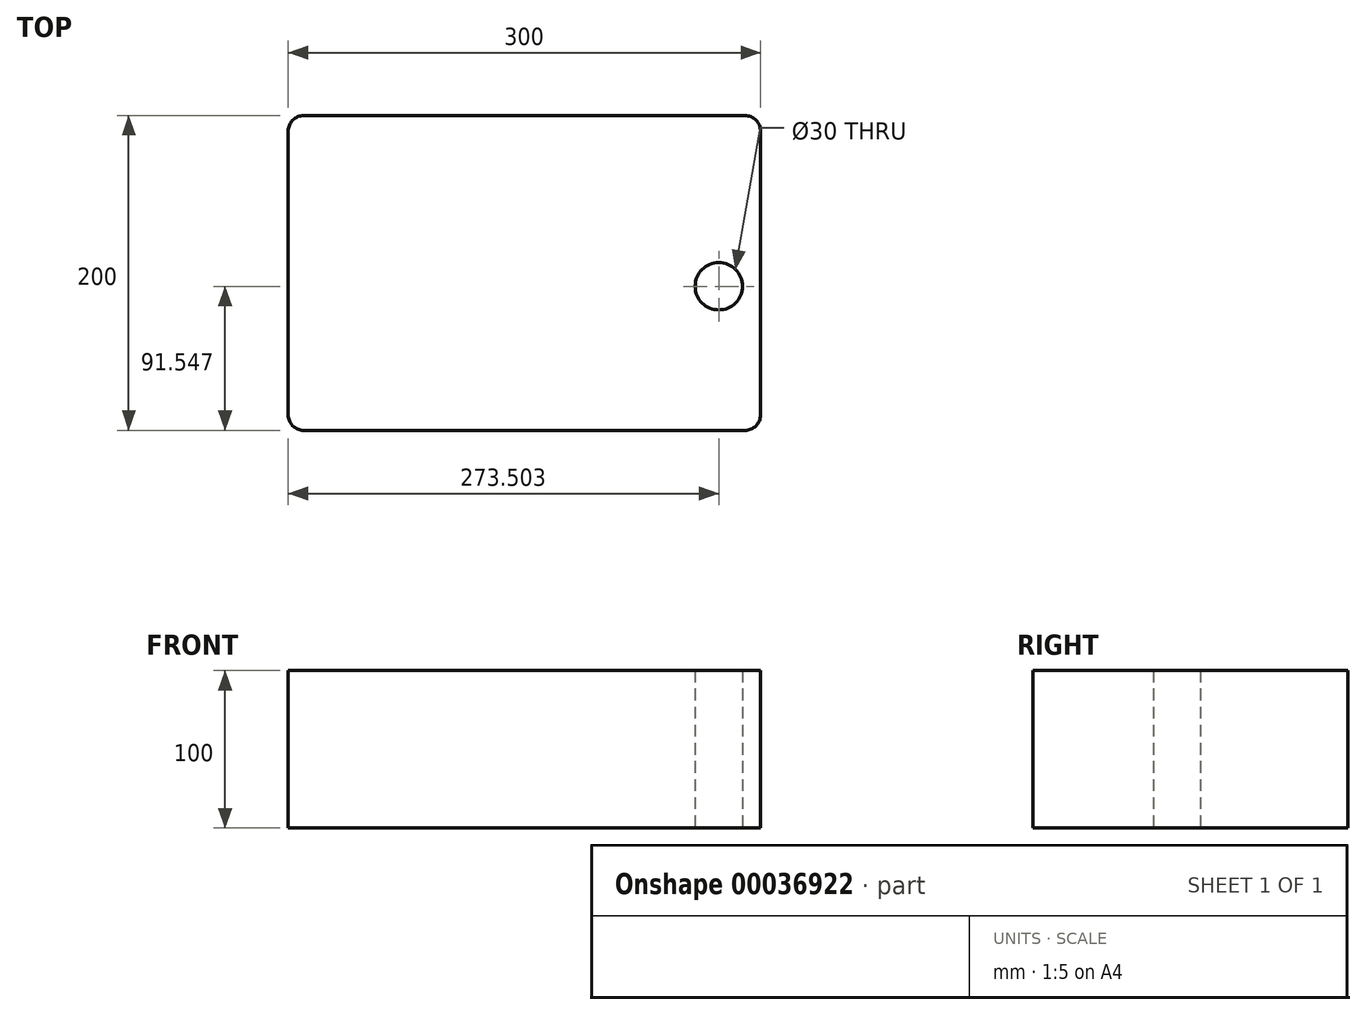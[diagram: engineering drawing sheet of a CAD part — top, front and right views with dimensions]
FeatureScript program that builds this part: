
annotation { "Feature Type Name" : "Feature", "Feature Type Description" : "" }
export const myFeature = defineFeature(function(context is Context, id is Id, definition is map)
    precondition{}
    {
        {
            var Q0;
            Q0=qCreatedBy(makeId("Top.planeOp"),FACE);
            var sketch = newSketch(context, id + "F0", { "sketchPlane" : qUnion([Q0])});
            skLineSegment(sketch, "E0.bottom", {"start": v(-149.02, 128.34) * mm, "end": v(150.98, 128.34) * mm});
            skLineSegment(sketch, "E0.top", {"start": v(-149.02, -71.66) * mm, "end": v(150.98, -71.66) * mm});
            skLineSegment(sketch, "E0.left", {"start": v(-149.02, 128.34) * mm, "end": v(-149.02, -71.66) * mm});
            skLineSegment(sketch, "E0.right", {"start": v(150.98, 128.34) * mm, "end": v(150.98, -71.66) * mm});
            skCircle(sketch, "E1", {"center": v(124.48, 19.89) * mm, "radius": 15 * mm});
            skSolve(sketch);
        }
        {
            var Q0;
            Q0=makeQuery(id+"F0.imprint","IMPRINT",FACE,{"disambiguationData":[TD([[makeQuery(id+"F0.imprint","IMPRINT",EDGE,{"derivedFrom":sQuery(id+"F0.wireOp",EDGE,"E0.bottom")}),-1.0]])]});
            extrude(context, id + "F1", {"entities" : qUnion([Q0]), "depth" : 100 * mm});
        }
        {
            var Q0;
            Q0=makeQuery(id+"F1.opExtrude","SWEPT_EDGE",EDGE,{"disambiguationData":[OSD([sQuery(id+"F0.wireOp",EDGE,"E0.bottom"),sQuery(id+"F0.wireOp",EDGE,"E0.left")])]});
            fillet(context, id + "F2", {"entities" : qUnion([Q0]), "radius" : 10 * mm, "tangentPropagation" : true, "allowEdgeOverflow" : false});
        }
        {
            var Q0;
            Q0=makeQuery(id+"F1.opExtrude","SWEPT_EDGE",EDGE,{"disambiguationData":[OSD([sQuery(id+"F0.wireOp",EDGE,"E0.bottom"),sQuery(id+"F0.wireOp",EDGE,"E0.right")])]});
            var Q1;
            Q1=makeQuery(id+"F1.opExtrude","SWEPT_EDGE",EDGE,{"disambiguationData":[OSD([sQuery(id+"F0.wireOp",EDGE,"E0.top"),sQuery(id+"F0.wireOp",EDGE,"E0.right")])]});
            var Q2;
            Q2=makeQuery(id+"F1.opExtrude","SWEPT_EDGE",EDGE,{"disambiguationData":[OSD([sQuery(id+"F0.wireOp",EDGE,"E0.top"),sQuery(id+"F0.wireOp",EDGE,"E0.left")])]});
            fillet(context, id + "F3", {"entities" : qUnion([Q0, Q1, Q2]), "radius" : 10 * mm, "tangentPropagation" : true, "allowEdgeOverflow" : false});
        }
    });
